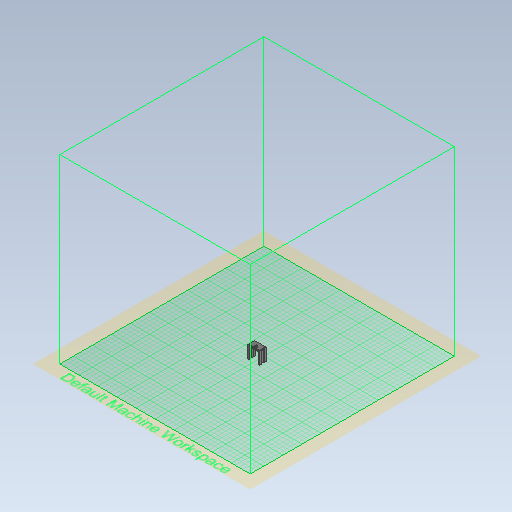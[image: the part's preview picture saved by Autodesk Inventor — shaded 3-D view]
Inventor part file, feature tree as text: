
AUTODESK INVENTOR PART (.ipt)
format: ipt  version: 2020 (Build 240168000, 168)  size: 500,736 bytes
history: native  units: mm
features: extrude x9, projected_geometry x6, sketch x4, fillet x2
ambient origin geometry x8: Origin, YZ Plane, XZ Plane, XY Plane, X Axis, Y Axis, Z Axis, Center Point
bodies: Body1 (feature_tree)
feature tree (21):
  extrude  "Выдавливание7"  Depth=4.0mm
  extrude  "Выдавливание16"  Depth=25.5mm
  sketch  "Эскиз12"
  extrude  "Выдавливание17"  Depth=3.0mm
  extrude  "Выдавливание18"  Depth=3.0mm
  extrude  "Выдавливание19"  Depth=3.0mm
  fillet  "Сопряжение1"  Radius=20.2mm
  extrude  "Выдавливание20"  Depth=14.0mm TaperAngle=0.0deg
  fillet  "Сопряжение2"  Radius=26.0mm
  extrude  "Выдавливание21"  Depth=20.5mm
  extrude  "Выдавливание22"  Depth=3.0mm
  extrude  "Выдавливание23"  Depth=1.5mm
  sketch  "Эскиз1"
  sketch  "Эскиз10"
  projected_geometry  "Спроецированная петля9"
  projected_geometry  "Спроецированная петля10"
  projected_geometry  "Спроецированная петля11"
  projected_geometry  "Спроецированная петля12"
  projected_geometry  "Спроецированная петля13"
  sketch  "Эскиз14"
  projected_geometry  "Спроецированная петля15"
